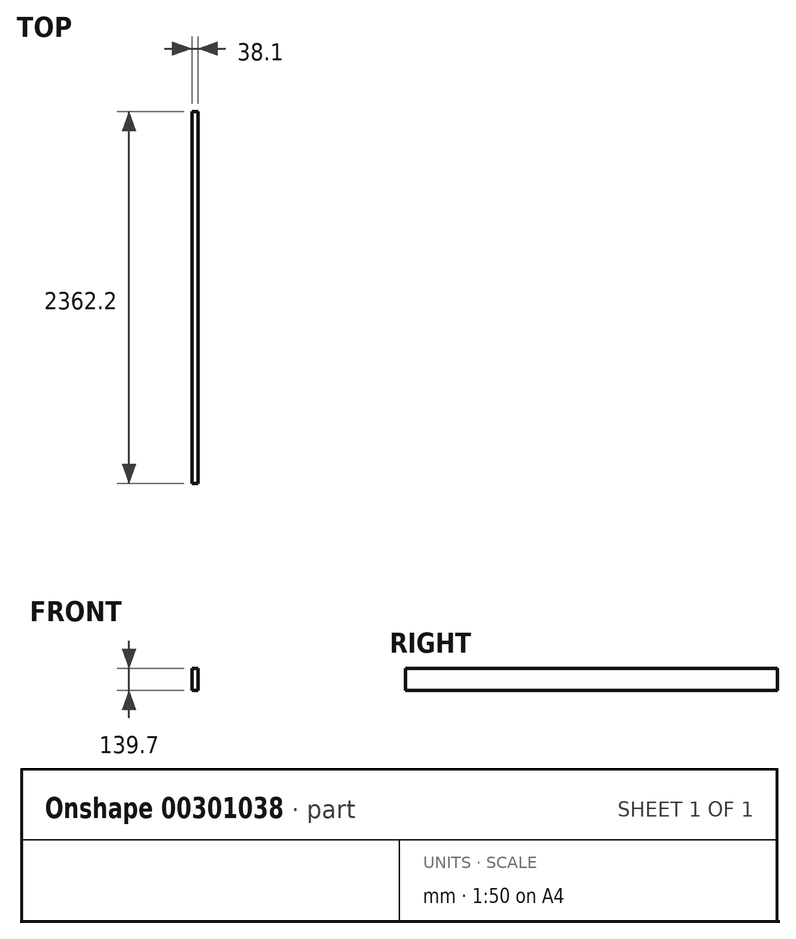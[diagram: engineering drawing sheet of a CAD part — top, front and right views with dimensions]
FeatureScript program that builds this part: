
annotation { "Feature Type Name" : "Feature", "Feature Type Description" : "" }
export const myFeature = defineFeature(function(context is Context, id is Id, definition is map)
    precondition{}
    {
        {
            var Q0;
            Q0=qCreatedBy(makeId("Front.planeOp"),FACE);
            var sketch = newSketch(context, id + "F0", { "sketchPlane" : qUnion([Q0])});
            skLineSegment(sketch, "E0.bottom", {"start": v(0, 0) * mm, "end": v(38.1, 0) * mm});
            skLineSegment(sketch, "E0.top", {"start": v(0, 139.7) * mm, "end": v(38.1, 139.7) * mm});
            skLineSegment(sketch, "E0.left", {"start": v(0, 0) * mm, "end": v(0, 139.7) * mm});
            skLineSegment(sketch, "E0.right", {"start": v(38.1, 0) * mm, "end": v(38.1, 139.7) * mm});
            skSolve(sketch);
        }
        {
            var Q0;
            Q0 = qSketchRegion(id + "F0", true);
            extrude(context, id + "F1", {"entities" : qUnion([Q0]), "oppositeDirection" : true, "depth" : 2362.2 * mm});
        }
    });
